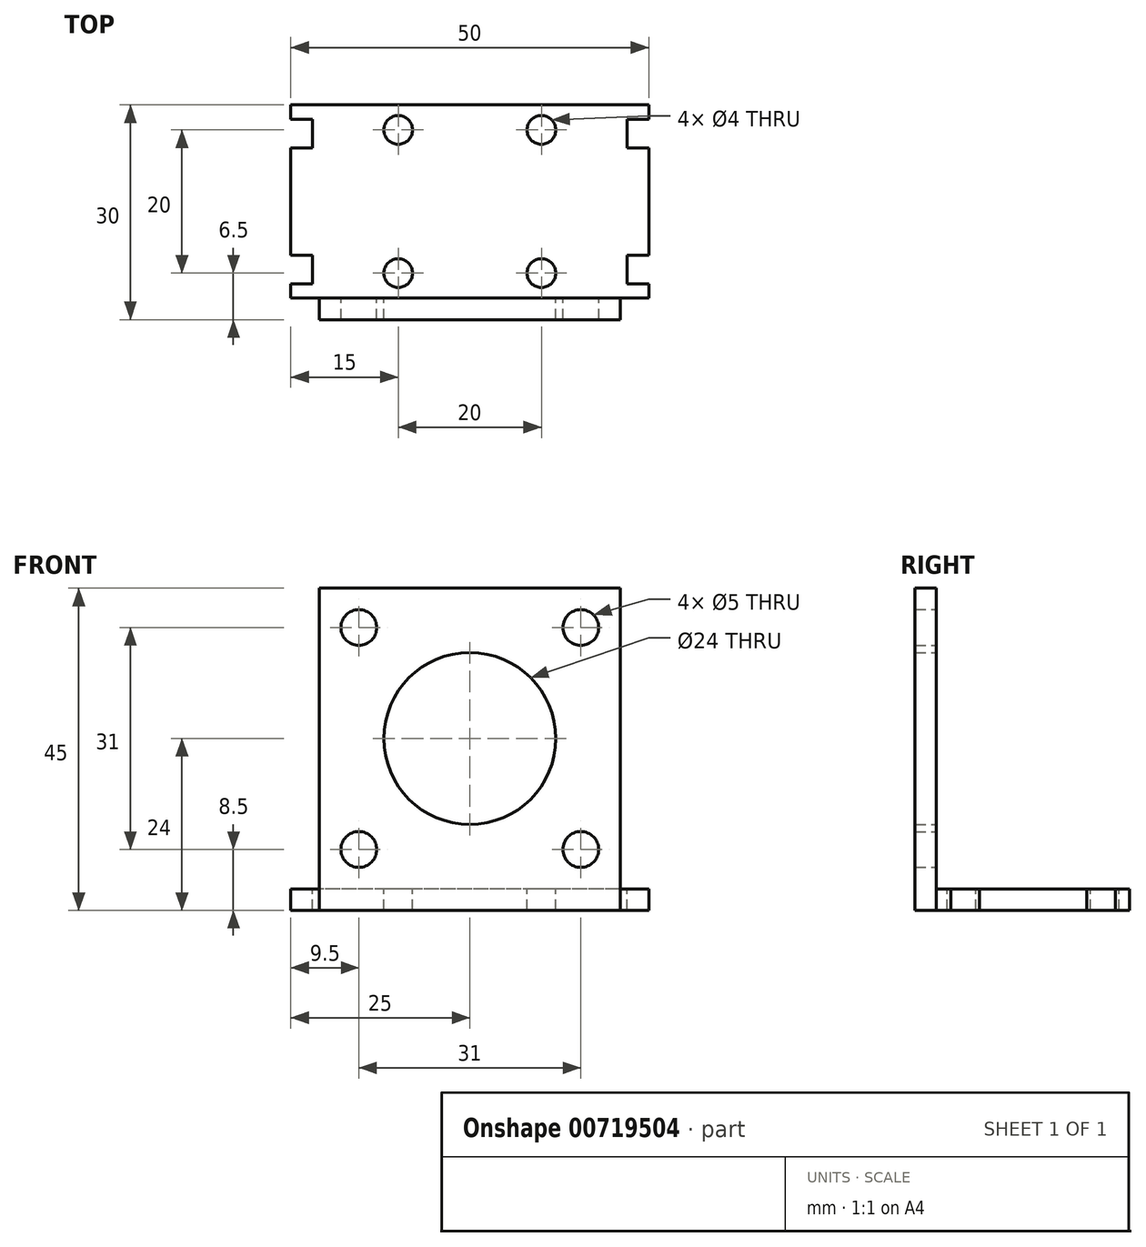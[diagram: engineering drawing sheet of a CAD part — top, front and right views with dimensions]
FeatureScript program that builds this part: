
annotation { "Feature Type Name" : "Feature", "Feature Type Description" : "" }
export const myFeature = defineFeature(function(context is Context, id is Id, definition is map)
    precondition{}
    {
        {
            var Q0;
            Q0=qCreatedBy(makeId("Top.planeOp"),FACE);
            var sketch = newSketch(context, id + "F0", { "sketchPlane" : qUnion([Q0])});
            skLineSegment(sketch, "E0.bottom", {"start": v(21, -15) * mm, "end": v(-21, -15) * mm});
            skLineSegment(sketch, "E0.top", {"start": v(21, 15) * mm, "end": v(-21, 15) * mm});
            skLineSegment(sketch, "E0.left", {"start": v(21, -15) * mm, "end": v(21, 15) * mm});
            skLineSegment(sketch, "E0.right", {"start": v(-21, -15) * mm, "end": v(-21, 15) * mm});
            skPoint(sketch, "E0.middle", {"position": v(0, 0) * mm});
            skLineSegment(sketch, "E1", {"start": v(21, -12) * mm, "end": v(-21, -12) * mm});
            skSolve(sketch);
        }
        {
            var Q0;
            {var subQ0=sQuery(id+"F0.wireOp",EDGE,"E0.top");Q0=makeQuery(id+"F0.imprint","IMPRINT",FACE,{"disambiguationData":[TD([[makeQuery(id+"F0.imprint","IMPRINT",EDGE,{"derivedFrom":subQ0}),1.0]])]});}
            extrude(context, id + "F1", {"entities" : qUnion([Q0]), "depth" : 3 * mm, "offsetDistance" : 25 * mm});
        }
        {
            var Q0;
            {var subQ0=sQuery(id+"F0.wireOp",EDGE,"E0.bottom");Q0=makeQuery(id+"F0.imprint","IMPRINT",FACE,{"disambiguationData":[TD([[makeQuery(id+"F0.imprint","IMPRINT",EDGE,{"derivedFrom":subQ0}),-1.0]])]});}
            extrude(context, id + "F2", {"entities" : qUnion([Q0]), "operationType" : NewBodyOperationType.ADD, "depth" : 45 * mm, "offsetDistance" : 25 * mm});
        }
        {
            var Q0;
            Q0=makeQuery(id+"F1.opExtrude","CAP_FACE",FACE,{"disambiguationData":[OSD([sQuery(id+"F0.wireOp",EDGE,"E0.top"),sQuery(id+"F0.wireOp",EDGE,"E0.left"),sQuery(id+"F0.wireOp",EDGE,"E0.right"),sQuery(id+"F0.wireOp",EDGE,"E1")])],"isStart":false});
            var sketch = newSketch(context, id + "F3", { "sketchPlane" : qUnion([Q0])});
            skLineSegment(sketch, "E2.bottom", {"start": v(10, -8.5) * mm, "end": v(-10, -8.5) * mm});
            skLineSegment(sketch, "E2.top", {"start": v(10, 11.5) * mm, "end": v(-10, 11.5) * mm});
            skLineSegment(sketch, "E2.left", {"start": v(10, -8.5) * mm, "end": v(10, 11.5) * mm});
            skLineSegment(sketch, "E2.right", {"start": v(-10, -8.5) * mm, "end": v(-10, 11.5) * mm});
            skSolve(sketch);
        }
        {
            var Q0;
            Q0=sQuery(id+"F3.wireOp",VERTEX,"E2.bottom.start");
            var Q1;
            Q1=sQuery(id+"F3.wireOp",VERTEX,"E2.left.end");
            var Q2;
            Q2=sQuery(id+"F3.wireOp",VERTEX,"E2.top.end");
            var Q3;
            Q3=sQuery(id+"F3.wireOp",VERTEX,"E2.right.start");
            var Q4;
            Q4=makeQuery(id+"F1.opExtrude","SWEPT_BODY",BODY,{"disambiguationData":[OSD([sQuery(id+"F0.wireOp",EDGE,"E0.top"),sQuery(id+"F0.wireOp",EDGE,"E0.left"),sQuery(id+"F0.wireOp",EDGE,"E0.right"),sQuery(id+"F0.wireOp",EDGE,"E1")])]});
            hole(context, id + "F4", {"style" : HoleStyle.SIMPLE, "endStyle" : HoleEndStyle.THROUGH, "holeDiameter" : 4 * mm, "majorDiameter" : 5 * mm, "isTappedThrough" : true, "tappedDepth" : 12 * mm, "tapClearance" : 3, "locations" : qUnion([Q0, Q1, Q2, Q3]), "scope" : qUnion([Q4])});
        }
        {
            var Q0;
            Q0=makeQuery(id+"F2.opExtrude","SWEPT_FACE",FACE,{"disambiguationData":[OSD([sQuery(id+"F0.wireOp",EDGE,"E1")])]});
            var sketch = newSketch(context, id + "F5", { "sketchPlane" : qUnion([Q0])});
            skLineSegment(sketch, "E3.bottom", {"start": v(15.5, 8.5) * mm, "end": v(-15.5, 8.5) * mm});
            skLineSegment(sketch, "E3.top", {"start": v(15.5, 39.5) * mm, "end": v(-15.5, 39.5) * mm});
            skLineSegment(sketch, "E3.left", {"start": v(15.5, 8.5) * mm, "end": v(15.5, 39.5) * mm});
            skLineSegment(sketch, "E3.right", {"start": v(-15.5, 8.5) * mm, "end": v(-15.5, 39.5) * mm});
            skPoint(sketch, "E3.middle", {"position": v(0, 24) * mm});
            skPoint(sketch, "E3.middle.positionSnap0", {"position": v(-21, 24) * mm});
            skPoint(sketch, "E3.centerSnap0", {"position": v(-21, 24) * mm});
            skSolve(sketch);
        }
        {
            var Q0;
            Q0=sQuery(id+"F5.wireOp",VERTEX,"E3.top.end");
            var Q1;
            Q1=sQuery(id+"F5.wireOp",VERTEX,"E3.bottom.end");
            var Q2;
            Q2=sQuery(id+"F5.wireOp",VERTEX,"E3.left.start");
            var Q3;
            Q3=sQuery(id+"F5.wireOp",VERTEX,"E3.top.start");
            var Q4;
            Q4=makeQuery(id+"F1.opExtrude","SWEPT_BODY",BODY,{"disambiguationData":[OSD([sQuery(id+"F0.wireOp",EDGE,"E0.top"),sQuery(id+"F0.wireOp",EDGE,"E0.left"),sQuery(id+"F0.wireOp",EDGE,"E0.right"),sQuery(id+"F0.wireOp",EDGE,"E1")])]});
            hole(context, id + "F6", {"style" : HoleStyle.SIMPLE, "endStyle" : HoleEndStyle.THROUGH, "holeDiameter" : 5 * mm, "majorDiameter" : 5 * mm, "isTappedThrough" : true, "tappedDepth" : 12 * mm, "tapClearance" : 3, "locations" : qUnion([Q0, Q1, Q2, Q3]), "scope" : qUnion([Q4])});
        }
        {
            var Q0;
            Q0=makeQuery(id+"F2.opExtrude","SWEPT_FACE",FACE,{"disambiguationData":[OSD([sQuery(id+"F0.wireOp",EDGE,"E1")])]});
            var sketch = newSketch(context, id + "F7", { "sketchPlane" : qUnion([Q0])});
            skCircle(sketch, "E4", {"center": v(0, 24) * mm, "radius": 12 * mm});
            skPoint(sketch, "E4.centerSnap0", {"position": v(0, 45) * mm});
            skPoint(sketch, "E4.centerSnap1", {"position": v(-21, 24) * mm});
            skSolve(sketch);
        }
        {
            var Q0;
            Q0=makeQuery(id+"F7.imprint","IMPRINT",FACE,{"disambiguationData":[TD([[makeQuery(id+"F7.imprint","IMPRINT",EDGE,{"derivedFrom":sQuery(id+"F7.wireOp",EDGE,"E4")}),1.0]])]});
            extrude(context, id + "F8", {"entities" : qUnion([Q0]), "operationType" : NewBodyOperationType.REMOVE, "oppositeDirection" : true, "depth" : 25 * mm, "offsetDistance" : 25 * mm});
        }
        {
            var Q0;
            {var subQ0=sQuery(id+"F0.wireOp",EDGE,"E0.right");Q0=makeQuery(id+"F2.boolean.opBoolean","MERGE",FACE,{"derivedFrom":[makeQuery(id+"F1.opExtrude","SWEPT_FACE",FACE,{"disambiguationData":[OSD([subQ0])]}),makeQuery(id+"F2.opExtrude","SWEPT_FACE",FACE,{"disambiguationData":[OSD([subQ0])]})]});}
            var sketch = newSketch(context, id + "F9", { "sketchPlane" : qUnion([Q0])});
            skPoint(sketch, "E5.oppositeSnap0", {"position": v(0, 0) * mm});
            skLineSegment(sketch, "E5.bottom", {"start": v(-15, 3) * mm, "end": v(12, 3) * mm});
            skLineSegment(sketch, "E5.top", {"start": v(-15, 0) * mm, "end": v(12, 0) * mm});
            skLineSegment(sketch, "E5.left", {"start": v(-15, 3) * mm, "end": v(-15, 0) * mm});
            skLineSegment(sketch, "E5.right", {"start": v(12, 3) * mm, "end": v(12, 0) * mm});
            skSolve(sketch);
        }
        {
            var Q0;
            Q0=makeQuery(id+"F9.imprint","IMPRINT",FACE,{"disambiguationData":[TD([[makeQuery(id+"F9.imprint","IMPRINT",EDGE,{"derivedFrom":sQuery(id+"F9.wireOp",EDGE,"E5.bottom")}),1.0]])]});
            extrude(context, id + "F10", {"entities" : qUnion([Q0]), "operationType" : NewBodyOperationType.ADD, "depth" : 4 * mm, "offsetDistance" : 25 * mm});
        }
        {
            var Q0;
            Q0=makeQuery(id+"F10.boolean.opBoolean","MERGE",FACE,{"derivedFrom":[makeQuery(id+"F1.opExtrude","CAP_FACE",FACE,{"disambiguationData":[OSD([sQuery(id+"F0.wireOp",EDGE,"E0.top"),sQuery(id+"F0.wireOp",EDGE,"E0.left"),sQuery(id+"F0.wireOp",EDGE,"E0.right"),sQuery(id+"F0.wireOp",EDGE,"E1")])],"isStart":false}),makeQuery(id+"F10.opExtrude","SWEPT_FACE",FACE,{"disambiguationData":[OSD([sQuery(id+"F9.wireOp",EDGE,"E5.bottom")])]})]});
            var sketch = newSketch(context, id + "F11", { "sketchPlane" : qUnion([Q0])});
            skPoint(sketch, "E6", {"position": v(-22, -6) * mm});
            skPoint(sketch, "E7", {"position": v(-22, 9) * mm});
            skLineSegment(sketch, "E8.bottom", {"start": v(-22, 9) * mm, "end": v(-25, 9) * mm});
            skLineSegment(sketch, "E8.top", {"start": v(-22, 13) * mm, "end": v(-25, 13) * mm});
            skLineSegment(sketch, "E8.left", {"start": v(-22, 9) * mm, "end": v(-22, 13) * mm});
            skLineSegment(sketch, "E8.right", {"start": v(-25, 9) * mm, "end": v(-25, 13) * mm});
            skLineSegment(sketch, "E9.bottom", {"start": v(-22, -6) * mm, "end": v(-25, -6) * mm});
            skLineSegment(sketch, "E9.top", {"start": v(-22, -10) * mm, "end": v(-25, -10) * mm});
            skLineSegment(sketch, "E9.left", {"start": v(-22, -6) * mm, "end": v(-22, -10) * mm});
            skLineSegment(sketch, "E9.right", {"start": v(-25, -6) * mm, "end": v(-25, -10) * mm});
            skSolve(sketch);
        }
        {
            var Q0;
            Q0=makeQuery(id+"F11.imprint","IMPRINT",FACE,{"disambiguationData":[TD([[makeQuery(id+"F11.imprint","IMPRINT",EDGE,{"derivedFrom":sQuery(id+"F11.wireOp",EDGE,"E8.bottom")}),-1.0]])]});
            var Q1;
            Q1 = qSketchRegion(id + "F11", true);
            var Q2;
            Q2=makeQuery(id+"F11.imprint","IMPRINT",FACE,{"disambiguationData":[TD([[makeQuery(id+"F11.imprint","IMPRINT",EDGE,{"derivedFrom":sQuery(id+"F11.wireOp",EDGE,"E9.bottom")}),1.0]])]});
            extrude(context, id + "F12", {"entities" : qUnion([Q0, Q1, Q2]), "operationType" : NewBodyOperationType.REMOVE, "oppositeDirection" : true, "depth" : 25 * mm, "offsetDistance" : 25 * mm});
        }
        {
            var Q0;
            {var subQ0=sQuery(id+"F0.wireOp",EDGE,"E0.left");Q0=makeQuery(id+"F2.boolean.opBoolean","MERGE",FACE,{"derivedFrom":[makeQuery(id+"F1.opExtrude","SWEPT_FACE",FACE,{"disambiguationData":[OSD([subQ0])]}),makeQuery(id+"F2.opExtrude","SWEPT_FACE",FACE,{"disambiguationData":[OSD([subQ0])]})]});}
            var sketch = newSketch(context, id + "F13", { "sketchPlane" : qUnion([Q0])});
            skLineSegment(sketch, "E10.bottom", {"start": v(-12, 3) * mm, "end": v(15, 3) * mm});
            skLineSegment(sketch, "E10.top", {"start": v(-12, 0) * mm, "end": v(15, 0) * mm});
            skLineSegment(sketch, "E10.left", {"start": v(-12, 3) * mm, "end": v(-12, 0) * mm});
            skLineSegment(sketch, "E10.right", {"start": v(15, 3) * mm, "end": v(15, 0) * mm});
            skSolve(sketch);
        }
        {
            var Q0;
            Q0 = qSketchRegion(id + "F13", true);
            extrude(context, id + "F14", {"entities" : qUnion([Q0]), "operationType" : NewBodyOperationType.ADD, "depth" : 4 * mm, "offsetDistance" : 25 * mm});
        }
        {
            var Q0;
            Q0=makeQuery(id+"F14.boolean.opBoolean","MERGE",FACE,{"derivedFrom":[makeQuery(id+"F10.boolean.opBoolean","MERGE",FACE,{"derivedFrom":[makeQuery(id+"F1.opExtrude","CAP_FACE",FACE,{"disambiguationData":[OSD([sQuery(id+"F0.wireOp",EDGE,"E0.top"),sQuery(id+"F0.wireOp",EDGE,"E0.left"),sQuery(id+"F0.wireOp",EDGE,"E0.right"),sQuery(id+"F0.wireOp",EDGE,"E1")])],"isStart":false}),makeQuery(id+"F10.opExtrude","SWEPT_FACE",FACE,{"disambiguationData":[OSD([sQuery(id+"F9.wireOp",EDGE,"E5.bottom")])]})]}),makeQuery(id+"F14.opExtrude","SWEPT_FACE",FACE,{"disambiguationData":[OSD([sQuery(id+"F13.wireOp",EDGE,"E10.bottom")])]})]});
            var sketch = newSketch(context, id + "F15", { "sketchPlane" : qUnion([Q0])});
            skLineSegment(sketch, "E11.bottom", {"start": v(25, 9) * mm, "end": v(22, 9) * mm});
            skLineSegment(sketch, "E11.top", {"start": v(25, 13) * mm, "end": v(22, 13) * mm});
            skLineSegment(sketch, "E11.left", {"start": v(25, 9) * mm, "end": v(25, 13) * mm});
            skLineSegment(sketch, "E11.right", {"start": v(22, 9) * mm, "end": v(22, 13) * mm});
            skLineSegment(sketch, "E12.bottom", {"start": v(25, -6) * mm, "end": v(22, -6) * mm});
            skLineSegment(sketch, "E12.top", {"start": v(25, -10) * mm, "end": v(22, -10) * mm});
            skLineSegment(sketch, "E12.left", {"start": v(25, -6) * mm, "end": v(25, -10) * mm});
            skLineSegment(sketch, "E12.right", {"start": v(22, -6) * mm, "end": v(22, -10) * mm});
            skSolve(sketch);
        }
        {
            var Q0;
            Q0=makeQuery(id+"F15.imprint","IMPRINT",FACE,{"disambiguationData":[TD([[makeQuery(id+"F15.imprint","IMPRINT",EDGE,{"derivedFrom":sQuery(id+"F15.wireOp",EDGE,"E11.bottom")}),-1.0]])]});
            var Q1;
            Q1=makeQuery(id+"F15.imprint","IMPRINT",FACE,{"disambiguationData":[TD([[makeQuery(id+"F15.imprint","IMPRINT",EDGE,{"derivedFrom":sQuery(id+"F15.wireOp",EDGE,"E12.bottom")}),1.0]])]});
            extrude(context, id + "F16", {"entities" : qUnion([Q0, Q1]), "operationType" : NewBodyOperationType.REMOVE, "oppositeDirection" : true, "depth" : 25 * mm, "offsetDistance" : 25 * mm});
        }
    });
